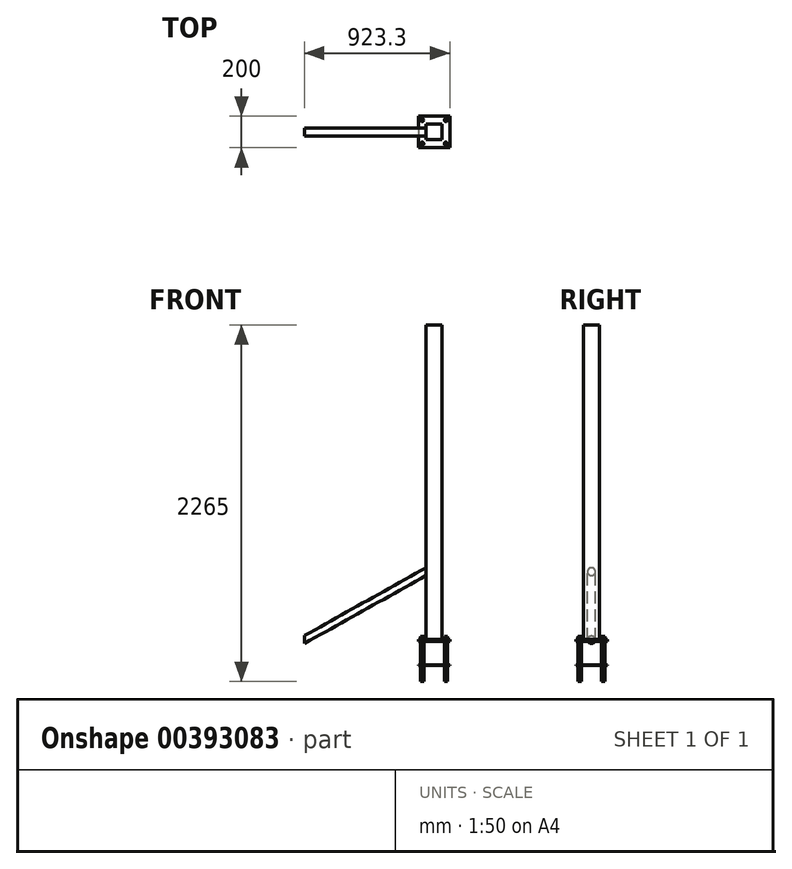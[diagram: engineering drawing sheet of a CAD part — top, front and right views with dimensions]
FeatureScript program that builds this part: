
annotation { "Feature Type Name" : "Feature", "Feature Type Description" : "" }
export const myFeature = defineFeature(function(context is Context, id is Id, definition is map)
    precondition{}
    {
        {
            var Q0;
            Q0=qCreatedBy(makeId("Top.planeOp"),FACE);
            var sketch = newSketch(context, id + "F0", { "sketchPlane" : qUnion([Q0])});
            skLineSegment(sketch, "E0.bottom", {"start": v(-50, -50) * mm, "end": v(50, -50) * mm});
            skLineSegment(sketch, "E0.top", {"start": v(-50, 50) * mm, "end": v(50, 50) * mm});
            skLineSegment(sketch, "E0.left", {"start": v(-50, -50) * mm, "end": v(-50, 50) * mm});
            skLineSegment(sketch, "E0.right", {"start": v(50, -50) * mm, "end": v(50, 50) * mm});
            skPoint(sketch, "E0.middle", {"position": v(0, 0) * mm});
            skSolve(sketch);
        }
        {
            var Q0;
            Q0 = qSketchRegion(id + "F0", true);
            extrude(context, id + "F1", {"entities" : qUnion([Q0]), "depth" : 2000 * mm});
        }
        {
            var Q0;
            Q0=makeQuery(id+"F1.opExtrude","CAP_FACE",FACE,{"disambiguationData":[OSD([sQuery(id+"F0.wireOp",EDGE,"E0.bottom"),sQuery(id+"F0.wireOp",EDGE,"E0.top"),sQuery(id+"F0.wireOp",EDGE,"E0.left"),sQuery(id+"F0.wireOp",EDGE,"E0.right")])],"isStart":true});
            var sketch = newSketch(context, id + "F2", { "sketchPlane" : qUnion([Q0])});
            skLineSegment(sketch, "E1.bottom", {"start": v(-100, -100) * mm, "end": v(100, -100) * mm});
            skLineSegment(sketch, "E1.top", {"start": v(-100, 100) * mm, "end": v(100, 100) * mm});
            skLineSegment(sketch, "E1.left", {"start": v(-100, -100) * mm, "end": v(-100, 100) * mm});
            skLineSegment(sketch, "E1.right", {"start": v(100, -100) * mm, "end": v(100, 100) * mm});
            skPoint(sketch, "E1.middle", {"position": v(0, 0) * mm});
            skSolve(sketch);
        }
        {
            var Q0;
            Q0 = qSketchRegion(id + "F2", true);
            extrude(context, id + "F3", {"entities" : qUnion([Q0]), "operationType" : NewBodyOperationType.ADD, "depth" : 12 * mm});
        }
        {
            var Q0;
            Q0=makeQuery(id+"F3.opExtrude","CAP_FACE",FACE,{"disambiguationData":[OSD([sQuery(id+"F2.wireOp",EDGE,"E1.bottom"),sQuery(id+"F2.wireOp",EDGE,"E1.top"),sQuery(id+"F2.wireOp",EDGE,"E1.left"),sQuery(id+"F2.wireOp",EDGE,"E1.right")])],"isStart":false});
            var sketch = newSketch(context, id + "F4", { "sketchPlane" : qUnion([Q0])});
            skLineSegment(sketch, "E2", {"start": v(-100, 100) * mm, "end": v(-75, 100) * mm});
            skLineSegment(sketch, "E3", {"start": v(-75, 100) * mm, "end": v(-75, 75) * mm});
            skLineSegment(sketch, "E4", {"start": v(-100, -100) * mm, "end": v(-75, -100) * mm});
            skLineSegment(sketch, "E5", {"start": v(-75, -100) * mm, "end": v(-75, -75) * mm});
            skLineSegment(sketch, "E6", {"start": v(100, -100) * mm, "end": v(75, -100) * mm});
            skLineSegment(sketch, "E7", {"start": v(75, -100) * mm, "end": v(75, -75) * mm});
            skLineSegment(sketch, "E8", {"start": v(100, 100) * mm, "end": v(75, 100) * mm});
            skLineSegment(sketch, "E9", {"start": v(75, 100) * mm, "end": v(75, 75) * mm});
            skCircle(sketch, "E10", {"center": v(-75, 75) * mm, "radius": 10 * mm});
            skCircle(sketch, "E11", {"center": v(75, 75) * mm, "radius": 10 * mm});
            skCircle(sketch, "E12", {"center": v(-75, -75) * mm, "radius": 10 * mm});
            skCircle(sketch, "E13", {"center": v(75, -75) * mm, "radius": 10 * mm});
            skSolve(sketch);
        }
        {
            var Q0;
            Q0 = qSketchRegion(id + "F4", true);
            extrude(context, id + "F5", {"entities" : qUnion([Q0]), "operationType" : NewBodyOperationType.ADD, "depth" : 150 * mm});
        }
        {
            var Q0;
            Q0=makeQuery(id+"F3.opExtrude","CAP_FACE",FACE,{"disambiguationData":[OSD([sQuery(id+"F2.wireOp",EDGE,"E1.bottom"),sQuery(id+"F2.wireOp",EDGE,"E1.top"),sQuery(id+"F2.wireOp",EDGE,"E1.left"),sQuery(id+"F2.wireOp",EDGE,"E1.right")])],"isStart":true});
            var sketch = newSketch(context, id + "F6", { "sketchPlane" : qUnion([Q0])});
            skLineSegment(sketch, "E14", {"start": v(-100, 100) * mm, "end": v(-75, 100) * mm});
            skLineSegment(sketch, "E15", {"start": v(-75, 100) * mm, "end": v(-75, 75) * mm});
            skLineSegment(sketch, "E16", {"start": v(-75, 75) * mm, "end": v(-75, -75) * mm});
            skLineSegment(sketch, "E17", {"start": v(100, 100) * mm, "end": v(75, 100) * mm});
            skLineSegment(sketch, "E18", {"start": v(75, 100) * mm, "end": v(75, 75) * mm});
            skLineSegment(sketch, "E19", {"start": v(75, 75) * mm, "end": v(75, -75) * mm});
            skCircle(sketch, "E20", {"center": v(-75, 75) * mm, "radius": 10 * mm});
            skCircle(sketch, "E21", {"center": v(75, 75) * mm, "radius": 10 * mm});
            skCircle(sketch, "E22", {"center": v(-75, -75) * mm, "radius": 10 * mm});
            skCircle(sketch, "E23", {"center": v(75, -75) * mm, "radius": 10 * mm});
            skSolve(sketch);
        }
        {
            var Q0;
            Q0 = qSketchRegion(id + "F6", true);
            extrude(context, id + "F7", {"entities" : qUnion([Q0]), "operationType" : NewBodyOperationType.ADD, "depth" : 20 * mm});
        }
        {
            var Q0;
            Q0=makeQuery(id+"F5.opExtrude","CAP_FACE",FACE,{"disambiguationData":[OSD([sQuery(id+"F4.wireOp",EDGE,"E10")])],"isStart":false});
            var sketch = newSketch(context, id + "F8", { "sketchPlane" : qUnion([Q0])});
            skLineSegment(sketch, "E24.bottom", {"start": v(-100, -100) * mm, "end": v(100, -100) * mm});
            skLineSegment(sketch, "E24.top", {"start": v(-100, 100) * mm, "end": v(100, 100) * mm});
            skLineSegment(sketch, "E24.left", {"start": v(-100, -100) * mm, "end": v(-100, 100) * mm});
            skLineSegment(sketch, "E24.right", {"start": v(100, -100) * mm, "end": v(100, 100) * mm});
            skPoint(sketch, "E24.middle", {"position": v(0, 0) * mm});
            skSolve(sketch);
        }
        {
            var Q0;
            Q0 = qSketchRegion(id + "F8", true);
            extrude(context, id + "F9", {"entities" : qUnion([Q0]), "operationType" : NewBodyOperationType.ADD, "depth" : 3 * mm});
        }
        {
            var Q0;
            Q0=makeQuery(id+"F9.opExtrude","CAP_FACE",FACE,{"disambiguationData":[OSD([sQuery(id+"F8.wireOp",EDGE,"E24.bottom"),sQuery(id+"F8.wireOp",EDGE,"E24.top"),sQuery(id+"F8.wireOp",EDGE,"E24.left"),sQuery(id+"F8.wireOp",EDGE,"E24.right")])],"isStart":false});
            var sketch = newSketch(context, id + "F10", { "sketchPlane" : qUnion([Q0])});
            skLineSegment(sketch, "E25", {"start": v(-100, 100) * mm, "end": v(-75, 100) * mm});
            skLineSegment(sketch, "E26", {"start": v(-75, 100) * mm, "end": v(-75, 75) * mm});
            skLineSegment(sketch, "E27", {"start": v(-75, 75) * mm, "end": v(-75, -75) * mm});
            skLineSegment(sketch, "E28", {"start": v(-75, -75) * mm, "end": v(75, -75) * mm});
            skLineSegment(sketch, "E29", {"start": v(75, -75) * mm, "end": v(75, 75) * mm});
            skCircle(sketch, "E30", {"center": v(-75, 75) * mm, "radius": 10 * mm});
            skCircle(sketch, "E31", {"center": v(75, 75) * mm, "radius": 10 * mm});
            skCircle(sketch, "E32", {"center": v(75, -75) * mm, "radius": 10 * mm});
            skCircle(sketch, "E33", {"center": v(-75, -75) * mm, "radius": 10 * mm});
            skSolve(sketch);
        }
        {
            var Q0;
            Q0 = qSketchRegion(id + "F10", true);
            extrude(context, id + "F11", {"entities" : qUnion([Q0]), "operationType" : NewBodyOperationType.ADD, "depth" : 100 * mm});
        }
        {
            var Q0;
            Q0=qCreatedBy(makeId("Front.planeOp"),FACE);
            var sketch = newSketch(context, id + "F12", { "sketchPlane" : qUnion([Q0])});
            skLineSegment(sketch, "E34", {"start": v(-823.67, 0) * mm, "end": v(-50.37, 431.62) * mm});
            skSolve(sketch);
        }
        {
            var Q0;
            Q0=makeQuery(id+"F1.opExtrude","SWEPT_FACE",FACE,{"disambiguationData":[OSD([sQuery(id+"F0.wireOp",EDGE,"E0.left")])]});
            var sketch = newSketch(context, id + "F13", { "sketchPlane" : qUnion([Q0])});
            skCircle(sketch, "E35", {"center": v(0, 431.85) * mm, "radius": 25 * mm});
            skSolve(sketch);
        }
        {
            var Q0;
            Q0=makeQuery(id+"F13.imprint","IMPRINT",FACE,{"disambiguationData":[TD([[makeQuery(id+"F13.imprint","IMPRINT",EDGE,{"derivedFrom":sQuery(id+"F13.wireOp",EDGE,"E35")}),1.0]])]});
            var Q1;
            Q1=sQuery(id+"F12.wireOp",EDGE,"E34");
            sweep(context, id + "F14", {"operationType" : NewBodyOperationType.ADD, "profiles" : qUnion([Q0]), "path" : qUnion([Q1])});
        }
    });
